# Revit family: Nivellierbare Kassette für Revisionsöffnung, RKN, 25, 9
name_source: partatom
category: Generic Models
revit_build: Autodesk Revit 2015 (Build: 20140606_1530(x64)
units: mm (PartAtom-declared; Revit-internal decimal feet)

## types (2) — shared parameters
Cut depth = 25 mm  [stored 0.082021 ft]
Height = 150 mm
Height 1 = 30 mm  [stored 0.0984252 ft]
HeightCalc = 150 mm
Length = 243 mm
Manufacturer = OBO Bettermann
URL = http://www.obo-bettermann.com
Width = 243 mm

## per-type parameters (varying)
| type | GTIN | Manufacturer Art.No. | Material |
| RKN2 9 VS 25 | 4012195867821 | 7409046 | Stainless Steel, Polished |
| RKN2 9 MS 25 | 4012195867647 | 7409024 | Brass, Soft Yellow, Welded |

note: column(s) folded — value = type name in every type: Article Type

note: [stored X ft] marks values corroborated as IEEE doubles in the binary element streams (Revit-internal decimal feet)

## geometry (parser evidence)
native form markers: Sweep x2
no freeform markers — native parametric forms only
